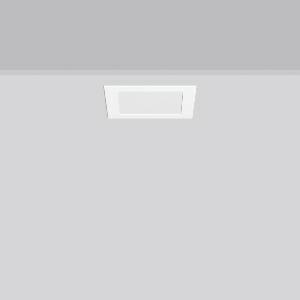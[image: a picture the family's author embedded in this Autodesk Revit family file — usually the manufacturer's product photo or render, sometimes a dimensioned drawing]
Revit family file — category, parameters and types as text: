
# Revit family: toledo_flat_square_e_901486_002_76_5ba2
name_source: partatom
category: Lighting Fixtures
units: mm (PartAtom-declared; Revit-internal decimal feet)

## family parameters
Cut with Voids When Loaded = No
Host = Face
Light Source = No
Part Type = Normal
Room Calculation Point = No
Round Connector Dimension = Use Diameter
Shared = No

## types (1)
- TOLEDO FLAT square E (1 x LED Modul 830, 770 lm, 3000)
    Apparent Load = 8 VA
    CIE Flux Codes = 49 80 96 100 100
    Color Rendering = 80
    Color Temperature = 3000
    Default Elevation = 1800 mm
    Description = Series: TOLEDO FLAT square
Ultra thin recessed downlight. Housing: die-cast aluminium. Light guide and diffuser made of non-yellowing PMMA, opal matt. Ceiling installation with spring system. Mounting depth depends on ceiling strength. Suitable for through-wiring with separately available accessories. Surface mounted housing as accessory for all sizes. Retrofittable decorative cylinders made of chintz fabric as accessory, optional with satin finish plastic diffuser. Through-wiring box (5 pole) available as accessory. 
Colour: white
Length: 172 mm
Width: 172 mm
Height: 3 mm
Cut-out length: 156 mm
Cut-out width: 156 mm
Recess height: 31-56 mm
Luminaire: recess height: 31-51 mm
Lamp: LED
Socket: without socket
Colour temperature: 3000K
Colour rendering index (CRI): 80
System power: 8 W
Rated luminous flux: 770 lm
Luminous efficiency: 96 lm/W
Control gear: Converter, dimmable, DALI
Protection class: II
Type of protection: IP 54
    Height = 0 mm  [stored 0 ft]
    Lamp = 1 x LED Modul 830
    Lamp Light Flux = 770 lm
    Lamp count = 1
    Length = 172 mm
    Lifetime = 50000 h
    Luminous efficacy = 96 lm/W
    Manufacturer = RZB
    ModVariant = No
    Model = 901486.002.76
    Mounting Place = Ceiling
    Mounting Type = Recessed
    Number of Poles = 1
    OnlyDefault = Yes
    Power Factor = 1
    Product Name = TOLEDO FLAT square E
    Product group = Recessed downlights
    ProductGroupID = 402
    Protection Class = Protection class II
    Protection Degree = IP 40
    RLX_Detail_Level = 1
    RLX_Emergency_Light_Flux = 0 lm
    RLX_Emergency_Type = 0
    RLX_Emergency_Type_DB = No
    RlxData = <blob elided: 57885 chars, md5=481214b1>
    Socket = socket
    Standby Power = 0 W
    System Light Flux = 770 lm
    System Power = 8 W
    Type Comments = Product without accessories
    Type Image = 901486.002.jpg
    URL = http://relux.com
    VarID = ---
    Voltage = 230 V
    Voltage Range = 220-240 V
    Weight = 0.00 kg
    Width = 172 mm

note: [stored X ft] marks values corroborated as IEEE doubles in the binary element streams (Revit-internal decimal feet)

## geometry (parser evidence)
native form markers: Blend x4, Sweep x10
no freeform markers — native parametric forms only
